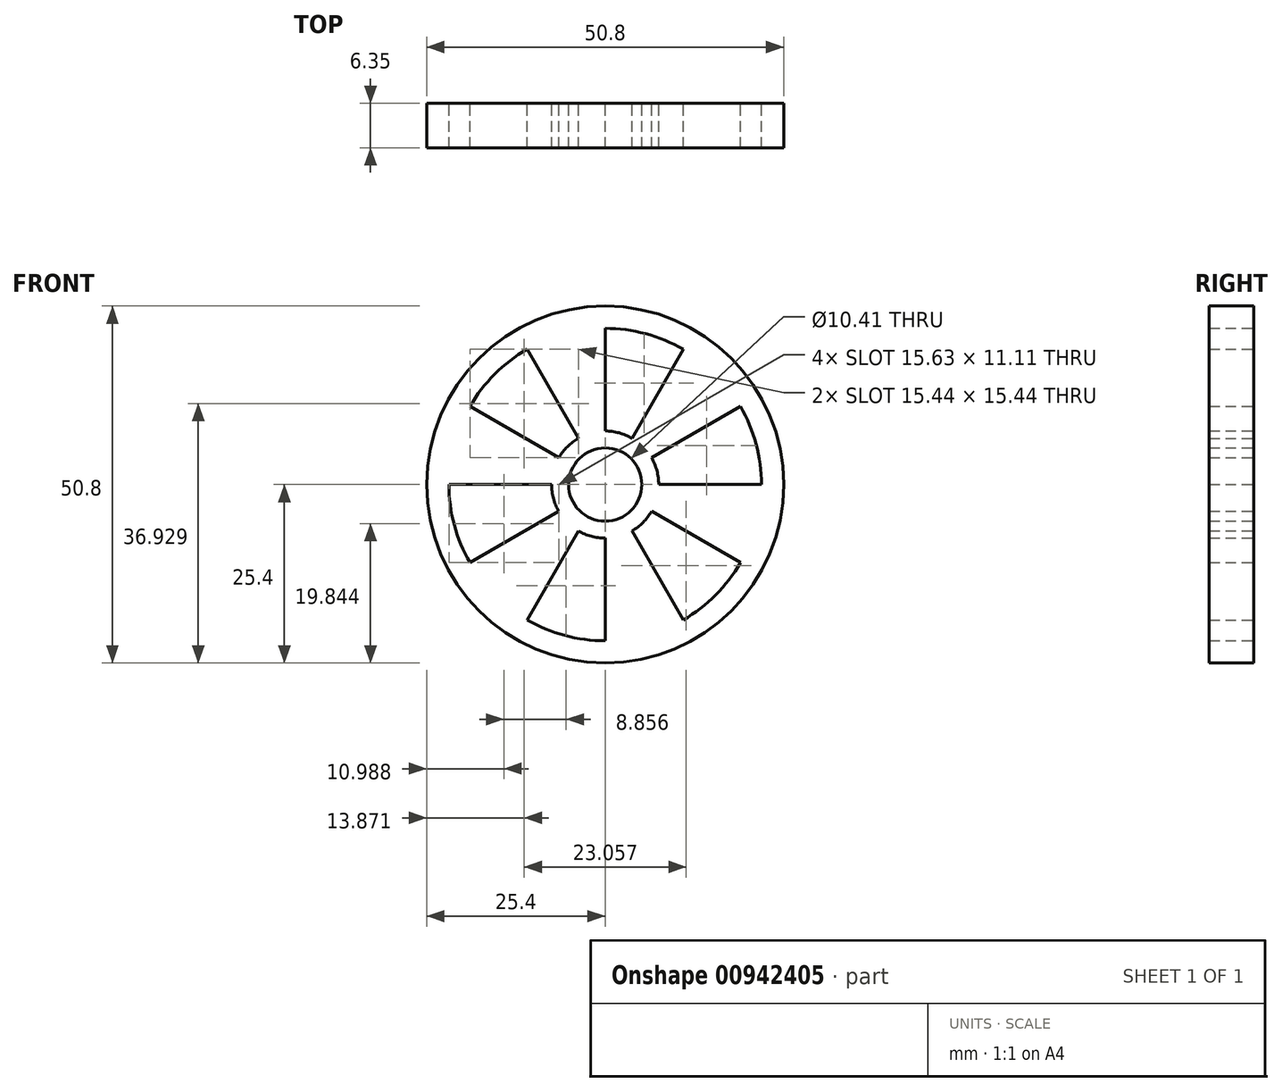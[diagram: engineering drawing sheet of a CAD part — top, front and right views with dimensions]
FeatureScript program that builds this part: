
annotation { "Feature Type Name" : "Feature", "Feature Type Description" : "" }
export const myFeature = defineFeature(function(context is Context, id is Id, definition is map)
    precondition{}
    {
        {
            var Q0;
            Q0=qCreatedBy(makeId("Front.planeOp"),FACE);
            var sketch = newSketch(context, id + "F0", { "sketchPlane" : qUnion([Q0])});
            skCircle(sketch, "E0", {"center": v(0, 0) * mm, "radius": 25.4 * mm});
            skCircle(sketch, "E1", {"center": v(0, 0) * mm, "radius": 22.23 * mm});
            skCircle(sketch, "E2", {"center": v(0, 0) * mm, "radius": 5.2 * mm});
            skCircle(sketch, "E3", {"center": v(0, 0) * mm, "radius": 7.62 * mm});
            skLineSegment(sketch, "E4", {"start": v(0, 22.23) * mm, "end": v(0, 7.62) * mm});
            skLineSegment(sketch, "E5.1.0", {"start": v(-11.11, 19.25) * mm, "end": v(-3.8, 6.6) * mm});
            skLineSegment(sketch, "E5.2.0", {"start": v(-19.25, 11.11) * mm, "end": v(-6.6, 3.81) * mm});
            skLineSegment(sketch, "E5.3.0", {"start": v(-22.23, 0) * mm, "end": v(-7.62, 0) * mm});
            skLineSegment(sketch, "E5.4.0", {"start": v(-19.25, -11.11) * mm, "end": v(-6.6, -3.8) * mm});
            skLineSegment(sketch, "E5.5.0", {"start": v(-11.11, -19.25) * mm, "end": v(-3.8, -6.6) * mm});
            skLineSegment(sketch, "E5.6.0", {"start": v(0, -22.23) * mm, "end": v(0, -7.62) * mm});
            skLineSegment(sketch, "E5.7.0", {"start": v(11.11, -19.25) * mm, "end": v(3.8, -6.6) * mm});
            skLineSegment(sketch, "E5.8.0", {"start": v(19.25, -11.11) * mm, "end": v(6.6, -3.81) * mm});
            skLineSegment(sketch, "E5.9.0", {"start": v(22.23, 0) * mm, "end": v(7.62, 0) * mm});
            skLineSegment(sketch, "E5.10.0", {"start": v(19.25, 11.11) * mm, "end": v(6.6, 3.81) * mm});
            skLineSegment(sketch, "E5.11.0", {"start": v(11.11, 19.25) * mm, "end": v(3.81, 6.6) * mm});
            skSolve(sketch);
        }
        {
            var Q0;
            {var subQ0=sQuery(id+"F0.wireOp",EDGE,"E5.10.0");Q0=makeQuery(id+"F0.imprint","IMPRINT",FACE,{"disambiguationData":[TD([[makeQuery(id+"F0.imprint","IMPRINT",EDGE,{"derivedFrom":subQ0}),-1.0]])]});}
            var Q1;
            {var subQ0=sQuery(id+"F0.wireOp",EDGE,"E4");Q1=makeQuery(id+"F0.imprint","IMPRINT",FACE,{"disambiguationData":[TD([[makeQuery(id+"F0.imprint","IMPRINT",EDGE,{"derivedFrom":subQ0}),-1.0]])]});}
            var Q2;
            {var subQ0=sQuery(id+"F0.wireOp",EDGE,"E5.2.0");Q2=makeQuery(id+"F0.imprint","IMPRINT",FACE,{"disambiguationData":[TD([[makeQuery(id+"F0.imprint","IMPRINT",EDGE,{"derivedFrom":subQ0}),-1.0]])]});}
            var Q3;
            {var subQ0=sQuery(id+"F0.wireOp",EDGE,"E5.4.0");Q3=makeQuery(id+"F0.imprint","IMPRINT",FACE,{"disambiguationData":[TD([[makeQuery(id+"F0.imprint","IMPRINT",EDGE,{"derivedFrom":subQ0}),-1.0]])]});}
            var Q4;
            {var subQ0=sQuery(id+"F0.wireOp",EDGE,"E5.6.0");Q4=makeQuery(id+"F0.imprint","IMPRINT",FACE,{"disambiguationData":[TD([[makeQuery(id+"F0.imprint","IMPRINT",EDGE,{"derivedFrom":subQ0}),-1.0]])]});}
            var Q5;
            {var subQ0=sQuery(id+"F0.wireOp",EDGE,"E5.8.0");Q5=makeQuery(id+"F0.imprint","IMPRINT",FACE,{"disambiguationData":[TD([[makeQuery(id+"F0.imprint","IMPRINT",EDGE,{"derivedFrom":subQ0}),-1.0]])]});}
            var Q6;
            Q6=makeQuery(id+"F0.imprint","IMPRINT",FACE,{"disambiguationData":[TD([[makeQuery(id+"F0.imprint","IMPRINT",EDGE,{"derivedFrom":sQuery(id+"F0.wireOp",EDGE,"E0")}),1.0]])]});
            var Q7;
            Q7=makeQuery(id+"F0.imprint","IMPRINT",FACE,{"disambiguationData":[TD([[makeQuery(id+"F0.imprint","IMPRINT",EDGE,{"derivedFrom":sQuery(id+"F0.wireOp",EDGE,"E2")}),-1.0]])]});
            extrude(context, id + "F1", {"entities" : qUnion([Q0, Q1, Q2, Q3, Q4, Q5, Q6, Q7]), "depth" : 6.35 * mm, "offsetDistance" : 25.4 * mm});
        }
    });
